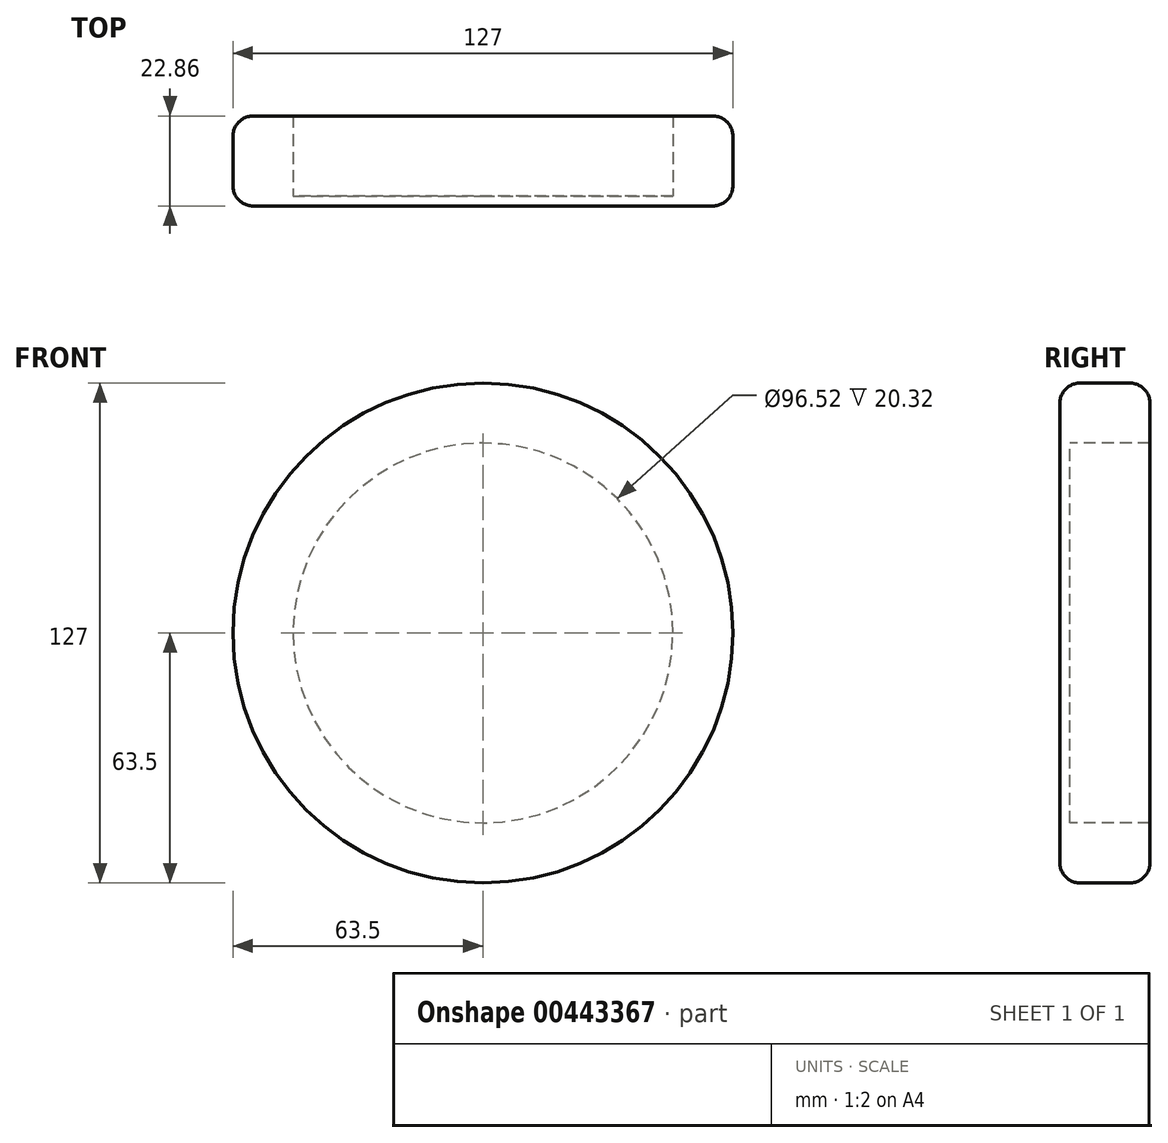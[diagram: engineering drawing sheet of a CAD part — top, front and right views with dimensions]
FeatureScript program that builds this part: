
annotation { "Feature Type Name" : "Feature", "Feature Type Description" : "" }
export const myFeature = defineFeature(function(context is Context, id is Id, definition is map)
    precondition{}
    {
        {
            var Q0;
            Q0=qCreatedBy(makeId("Front.planeOp"),FACE);
            var sketch = newSketch(context, id + "F0", { "sketchPlane" : qUnion([Q0])});
            skCircle(sketch, "E0", {"center": v(0, 0) * mm, "radius": 63.5 * mm});
            skCircle(sketch, "E1", {"center": v(0, 0) * mm, "radius": 48.26 * mm});
            skCircle(sketch, "E2.cCircle", {"center": v(0, 0) * mm, "radius": 43.48 * mm, "construction": true});
            skLineSegment(sketch, "E2.0", {"start": v(44.9, -17.68) * mm, "end": v(14.17, -46.13) * mm});
            skLineSegment(sketch, "E2.1", {"start": v(14.17, -46.13) * mm, "end": v(-27.23, -39.84) * mm});
            skLineSegment(sketch, "E2.2", {"start": v(-27.23, -39.84) * mm, "end": v(-48.13, -3.55) * mm});
            skLineSegment(sketch, "E2.3", {"start": v(-48.13, -3.55) * mm, "end": v(-32.79, 35.41) * mm});
            skLineSegment(sketch, "E2.4", {"start": v(-32.79, 35.41) * mm, "end": v(7.25, 47.71) * mm});
            skLineSegment(sketch, "E2.5", {"start": v(7.25, 47.71) * mm, "end": v(41.82, 24.08) * mm});
            skLineSegment(sketch, "E2.6", {"start": v(41.82, 24.08) * mm, "end": v(44.9, -17.68) * mm});
            skPoint(sketch, "E2.0.midPoint", {"position": v(29.54, -31.9) * mm});
            skSolve(sketch);
        }
        {
            var Q0;
            Q0 = qSketchRegion(id + "F0", true);
            extrude(context, id + "F1", {"entities" : qUnion([Q0]), "oppositeDirection" : true, "depth" : 20.32 * mm});
        }
        {
            var Q0;
            Q0=qCreatedBy(makeId("Front.planeOp"),FACE);
            var sketch = newSketch(context, id + "F2", { "sketchPlane" : qUnion([Q0])});
            skCircle(sketch, "E3", {"center": v(0, 0) * mm, "radius": 63.5 * mm});
            skSolve(sketch);
        }
        {
            var Q0;
            Q0 = qSketchRegion(id + "F2", true);
            extrude(context, id + "F3", {"entities" : qUnion([Q0]), "operationType" : NewBodyOperationType.ADD, "depth" : 2.54 * mm});
        }
        {
            var Q0;
            Q0=makeQuery(id+"F3.opExtrude","CAP_EDGE",EDGE,{"disambiguationData":[OSD([sQuery(id+"F2.wireOp",EDGE,"E3")])],"isStart":false});
            var Q1;
            Q1=makeQuery(id+"F3.boolean.opBoolean","MERGE",FACE,{"derivedFrom":[makeQuery(id+"F1.opExtrude","SWEPT_FACE",FACE,{"disambiguationData":[OSD([sQuery(id+"F0.wireOp",EDGE,"E0")])]}),makeQuery(id+"F3.opExtrude","SWEPT_FACE",FACE,{"disambiguationData":[OSD([sQuery(id+"F2.wireOp",EDGE,"E3")])]})]});
            fillet(context, id + "F4", {"entities" : qUnion([Q0, Q1]), "radius" : 5.08 * mm, "tangentPropagation" : true, "allowEdgeOverflow" : false});
        }
    });
